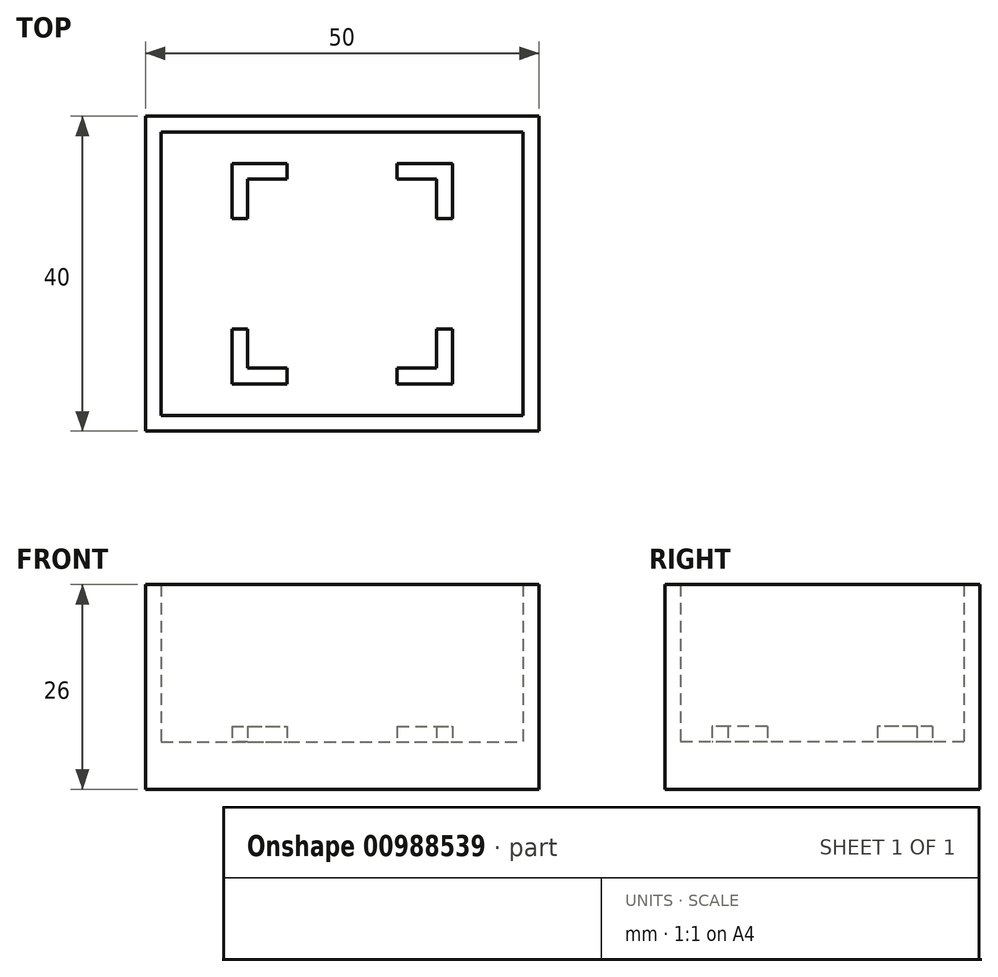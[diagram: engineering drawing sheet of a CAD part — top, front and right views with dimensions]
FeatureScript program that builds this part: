
annotation { "Feature Type Name" : "Feature", "Feature Type Description" : "" }
export const myFeature = defineFeature(function(context is Context, id is Id, definition is map)
    precondition{}
    {
        {
            var Q0;
            Q0=qCreatedBy(makeId("Top.planeOp"),FACE);
            var sketch = newSketch(context, id + "F0", { "sketchPlane" : qUnion([Q0])});
            skLineSegment(sketch, "E0.bottom", {"start": v(-25, 20) * mm, "end": v(25, 20) * mm});
            skLineSegment(sketch, "E0.top", {"start": v(-25, -20) * mm, "end": v(25, -20) * mm});
            skLineSegment(sketch, "E0.left", {"start": v(-25, 20) * mm, "end": v(-25, -20) * mm});
            skLineSegment(sketch, "E0.right", {"start": v(25, 20) * mm, "end": v(25, -20) * mm});
            skPoint(sketch, "E0.middle", {"position": v(0, 0) * mm});
            skSolve(sketch);
        }
        {
            var Q0;
            Q0=makeQuery(id+"F0.imprint","IMPRINT",FACE,{"disambiguationData":[TD([[makeQuery(id+"F0.imprint","IMPRINT",EDGE,{"derivedFrom":sQuery(id+"F0.wireOp",EDGE,"E0.bottom")}),-1.0]])]});
            extrude(context, id + "F1", {"entities" : qUnion([Q0]), "depth" : 6 * mm, "offsetDistance" : 25 * mm});
        }
        {
            var Q0;
            Q0=makeQuery(id+"F1.opExtrude","CAP_FACE",FACE,{"disambiguationData":[OSD([sQuery(id+"F0.wireOp",EDGE,"E0.bottom"),sQuery(id+"F0.wireOp",EDGE,"E0.top"),sQuery(id+"F0.wireOp",EDGE,"E0.left"),sQuery(id+"F0.wireOp",EDGE,"E0.right")])],"isStart":false});
            var sketch = newSketch(context, id + "F2", { "sketchPlane" : qUnion([Q0])});
            skLineSegment(sketch, "E1.bottom", {"start": v(-23, 18) * mm, "end": v(23, 18) * mm});
            skLineSegment(sketch, "E1.top", {"start": v(-23, -18) * mm, "end": v(23, -18) * mm});
            skLineSegment(sketch, "E1.left", {"start": v(-23, 18) * mm, "end": v(-23, -18) * mm});
            skLineSegment(sketch, "E1.right", {"start": v(23, 18) * mm, "end": v(23, -18) * mm});
            skPoint(sketch, "E1.middle", {"position": v(0, 0) * mm});
            skSolve(sketch);
        }
        {
            var Q0;
            Q0=makeQuery(id+"F2.imprint","IMPRINT",FACE,{"disambiguationData":[TD([[makeQuery(id+"F2.imprint","IMPRINT",EDGE,{"derivedFrom":sQuery(id+"F2.wireOp",EDGE,"E1.bottom")}),1.0]])]});
            extrude(context, id + "F3", {"entities" : qUnion([Q0]), "operationType" : NewBodyOperationType.ADD, "depth" : 20 * mm, "offsetDistance" : 25 * mm});
        }
        {
            var Q0;
            Q0=makeQuery(id+"F1.opExtrude","CAP_FACE",FACE,{"disambiguationData":[OSD([sQuery(id+"F0.wireOp",EDGE,"E0.bottom"),sQuery(id+"F0.wireOp",EDGE,"E0.top"),sQuery(id+"F0.wireOp",EDGE,"E0.left"),sQuery(id+"F0.wireOp",EDGE,"E0.right")])],"isStart":false});
            var sketch = newSketch(context, id + "F4", { "sketchPlane" : qUnion([Q0])});
            skLineSegment(sketch, "E2.bottom", {"start": v(-12, 12) * mm, "end": v(-7, 12) * mm});
            skLineSegment(sketch, "E2.top", {"start": v(-12, -12) * mm, "end": v(-7, -12) * mm});
            skLineSegment(sketch, "E2.left", {"start": v(-12, 12) * mm, "end": v(-12, 7) * mm});
            skLineSegment(sketch, "E2.right", {"start": v(12, 12) * mm, "end": v(12, 7) * mm});
            skPoint(sketch, "E2.middle", {"position": v(0, 0) * mm});
            skLineSegment(sketch, "E3.bottom", {"start": v(-14, 14) * mm, "end": v(-7, 14) * mm});
            skLineSegment(sketch, "E3.top", {"start": v(-14, -14) * mm, "end": v(-7, -14) * mm});
            skLineSegment(sketch, "E3.left", {"start": v(-14, 14) * mm, "end": v(-14, 7) * mm});
            skLineSegment(sketch, "E3.right", {"start": v(14, 14) * mm, "end": v(14, 7) * mm});
            skLineSegment(sketch, "E4", {"start": v(-7, 14) * mm, "end": v(-7, 12) * mm});
            skLineSegment(sketch, "E5", {"start": v(7, 14) * mm, "end": v(7, 12) * mm});
            skLineSegment(sketch, "E6", {"start": v(12, 7) * mm, "end": v(14, 7) * mm});
            skLineSegment(sketch, "E7", {"start": v(12, -7) * mm, "end": v(14, -7) * mm});
            skLineSegment(sketch, "E8", {"start": v(7, -12) * mm, "end": v(7, -14) * mm});
            skLineSegment(sketch, "E9", {"start": v(-7, -12) * mm, "end": v(-7, -14) * mm});
            skLineSegment(sketch, "E10", {"start": v(-12, -7) * mm, "end": v(-14, -7) * mm});
            skLineSegment(sketch, "E11", {"start": v(-14, 7) * mm, "end": v(-12, 7) * mm});
            skLineSegment(sketch, "E12.trimOffspring", {"start": v(7, 14) * mm, "end": v(14, 14) * mm});
            skLineSegment(sketch, "E13.trimOffspring", {"start": v(7, 12) * mm, "end": v(12, 12) * mm});
            skLineSegment(sketch, "E14.trimOffspring", {"start": v(-12, -7) * mm, "end": v(-12, -12) * mm});
            skLineSegment(sketch, "E15.trimOffspring", {"start": v(-14, -7) * mm, "end": v(-14, -14) * mm});
            skLineSegment(sketch, "E16.trimOffspring", {"start": v(12, -7) * mm, "end": v(12, -12) * mm});
            skLineSegment(sketch, "E17.trimOffspring", {"start": v(14, -7) * mm, "end": v(14, -14) * mm});
            skLineSegment(sketch, "E18.trimOffspring", {"start": v(7, -14) * mm, "end": v(14, -14) * mm});
            skLineSegment(sketch, "E19.trimOffspring", {"start": v(7, -12) * mm, "end": v(12, -12) * mm});
            skSolve(sketch);
        }
        {
            var Q0;
            Q0=makeQuery(id+"F4.imprint","IMPRINT",FACE,{"disambiguationData":[TD([[makeQuery(id+"F4.imprint","IMPRINT",EDGE,{"derivedFrom":sQuery(id+"F4.wireOp",EDGE,"E2.bottom")}),1.0]])]});
            var Q1;
            Q1=makeQuery(id+"F4.imprint","IMPRINT",FACE,{"disambiguationData":[TD([[makeQuery(id+"F4.imprint","IMPRINT",EDGE,{"derivedFrom":sQuery(id+"F4.wireOp",EDGE,"E2.right")}),1.0]])]});
            var Q2;
            Q2=makeQuery(id+"F4.imprint","IMPRINT",FACE,{"disambiguationData":[TD([[makeQuery(id+"F4.imprint","IMPRINT",EDGE,{"derivedFrom":sQuery(id+"F4.wireOp",EDGE,"E7")}),-1.0]])]});
            var Q3;
            Q3=makeQuery(id+"F4.imprint","IMPRINT",FACE,{"disambiguationData":[TD([[makeQuery(id+"F4.imprint","IMPRINT",EDGE,{"derivedFrom":sQuery(id+"F4.wireOp",EDGE,"E2.top")}),-1.0]])]});
            extrude(context, id + "F5", {"entities" : qUnion([Q0, Q1, Q2, Q3]), "operationType" : NewBodyOperationType.ADD, "depth" : 2 * mm, "offsetDistance" : 25 * mm});
        }
    });
